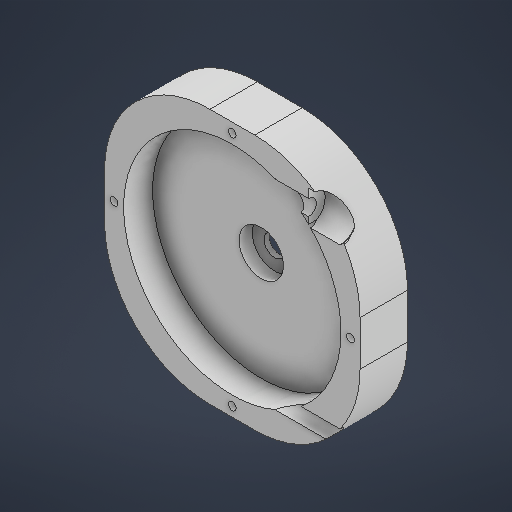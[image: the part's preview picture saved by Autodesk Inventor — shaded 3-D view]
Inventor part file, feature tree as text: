
AUTODESK INVENTOR PART (.ipt)
format: ipt  version: 2025.3 (Build 293356030, 356C)  size: 307,200 bytes
history: native  units: mm
features: sketch x4, extrude x4, revolve x2, projected_geometry x2
ambient origin geometry x8: Origin, YZ Plane, XZ Plane, XY Plane, X Axis, Y Axis, Z Axis, Center Point
bodies: Solid1 (feature_tree)
feature tree (12):
  sketch  "Sketch1"  dims[d0=97.0mm d1=82.5mm]
  extrude  "Extrusion1"  Depth=82.5mm
  extrude  "Extrusion2"  Depth=8.0mm
  extrude  "Extrusion3"  Depth=7.0mm TaperAngle=0.0deg
  sketch  "Sketch3"  dims[d4=2.0mm d5=0.0mm d6=7.0mm d7=0.0mm]
  revolve  "Revolution1"  [1 undecoded]
  revolve  "Revolution2"  [1 undecoded]
  extrude  "Extrusion4"  Depth=18.0mm
  sketch  "Sketch4"  dims[d8=18.0mm d9=0.0mm d10=40.0mm d12=10.65mm d13=14.65mm d14=12.65mm d15=45.0deg d16=45.0deg d17=15.0mm d18=6.0mm d19=12.0mm d20=360.0deg d21=7.0mm d22=6.0mm d24=90.0deg d25=2.97mm d26=40.0mm d28=360.0deg d30=0.0mm d31=0.0mm]
  projected_geometry  "Projected Loop1"
  projected_geometry  "Projected Loop2"
  sketch  "Sketch Circular Pattern1"  dims[d2=16.9mm d3=8.0mm]
note: 2 required parameter values undecoded (feature->parameter linkage not recoverable at this tier; creation-order binding heuristic only, values carry confidence <= 0.55)
